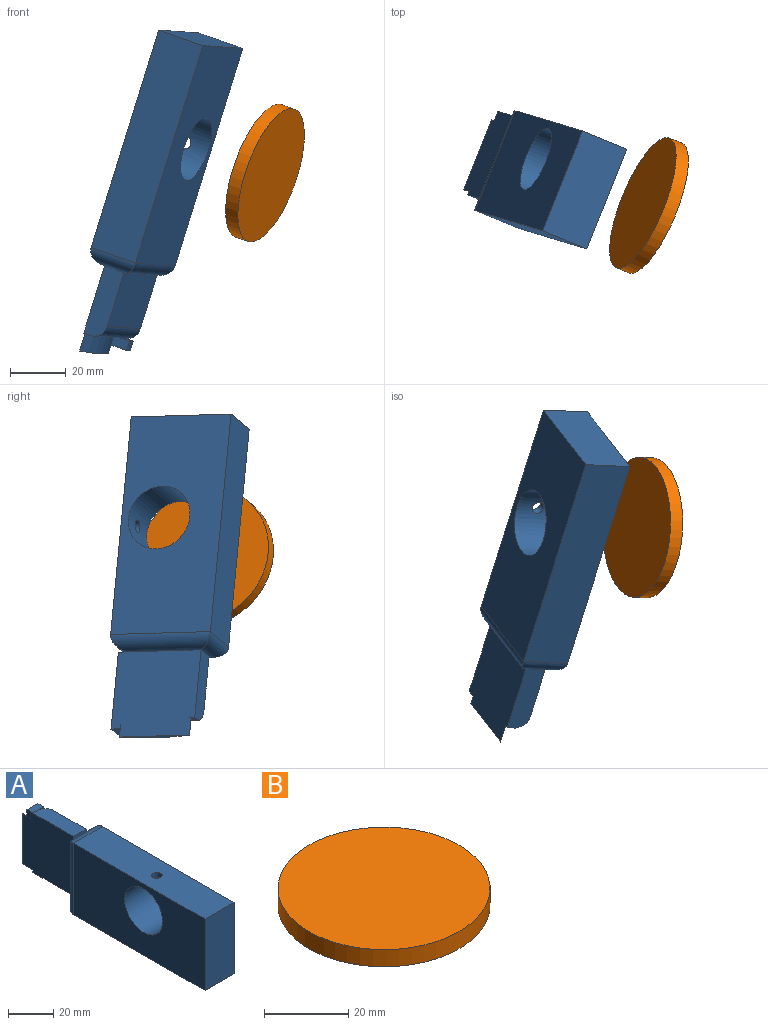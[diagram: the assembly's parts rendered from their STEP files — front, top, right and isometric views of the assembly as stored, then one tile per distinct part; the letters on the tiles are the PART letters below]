
ASSEMBLY  parts=2 mates=1
PART A: 26 faces, bbox 18.1x119.4x38.6 mm
  f0: plane 32.16x32.08mm, normal (-1,0,0), area 1009.8mm2, adj f1,f3,f4,f5,f13,f18,f20,f21
  f1: plane 6.69x3.63mm, normal (0,1,0), area 24.2mm2, adj f0,f2,f23,f24,f25
  f2: plane 3.64x3.63mm, normal (1,0,0), area 13.2mm2, adj f1,f3,f24,f25
  f3: plane 6.69x3.63mm, normal (0,-1,0), area 14.1mm2, adj f0,f2,f19,f21,f24,f25
  f4: plane 27.11x2.01mm, normal (0,1,0), area 37.6mm2, adj f0,f22,f23
  f5: plane 28.45x2.83mm, normal (0,1,0), area 42.8mm2, adj f0,f18,f19,f22,f24
  f6: plane 82.14x38.61mm, normal (-1,0,0), area 2730.3mm2, adj f7,f9,f10,f11,f13
  f7: plane 38.61x18.07mm, normal (0,-1,0), area 697.6mm2, adj f6,f8,f9,f10
  f8: plane 82.14x38.61mm, normal (1,0,0), area 2730.3mm2, adj f7,f9,f10,f11,f16
  f9: plane 82.14x18.07mm, normal (0,0,1), area 1467.3mm2, adj f6,f7,f8,f12,f14
  f10: plane 82.14x18.07mm, normal (0,0,-1), area 1483.9mm2, adj f6,f7,f8,f15
  f11: cylinder r=11.85mm len=23.7mm, axis (-1,0,0), area 1328.4mm2, adj f6,f8,f12
  f12: cylinder r=2.3mm len=4.6mm, axis (0,0,1), area 40.8mm2, adj f9,f11
  f13: cylinder r=5.08mm len=38.61mm, axis (0,0,1), area 278.6mm2, adj f0,f6,f14,f15
  f14: cylinder r=5.08mm len=18.07mm, axis (1,0,0), area 114.7mm2, adj f9,f13,f16,f20
  f15: cylinder r=5.08mm len=18.07mm, axis (-1,0,0), area 114.7mm2, adj f10,f13,f16,f18
  f16: cylinder r=5.08mm len=38.61mm, axis (0,0,-1), area 278.6mm2, adj f8,f14,f15,f17
  f17: plane 32.03x20.32mm, normal (1,0,0), area 650.8mm2, adj f16,f18,f19,f20,f21
  f18: plane 25.4x7.91mm, normal (0,0,-1), area 195.3mm2, adj f0,f5,f15,f17,f19
  f19: cylinder r=5.08mm len=32.03mm, axis (0,0,1), area 255.6mm2, adj f3,f5,f17,f18,f21
  f20: plane 7.91x3.57mm, normal (0,-1,0), area 28.3mm2, adj f0,f14,f17,f21
  f21: plane 25.4x7.91mm, normal (0,0,1), area 195.3mm2, adj f0,f3,f17,f19,f20
  f22: cylinder r=49.9mm len=27.09mm, axis (0,-1,0), area 185.5mm2, adj f0,f4,f5,f23,f24
  f23: plane 3.12x0.27mm, normal (0.07,0,1), area 0.8mm2, adj f0,f1,f4,f22
  f24: plane 6.42x3.64mm, normal (0,0,-1), area 23.4mm2, adj f1,f2,f3,f5,f22
  f25: plane 6.69x3.64mm, normal (0,0,1), area 24.3mm2, adj f0,f1,f2,f3
PART B: 3 faces, bbox 50.4x50.4x5 mm
  f0: cylinder r=25.19mm len=50.39mm, axis (0,0,1), area 791.5mm2, adj f1,f2
  f1: plane 50.39x50.39mm, normal (0,0,1), area 1994mm2, adj f0
  f2: plane 50.39x50.39mm, normal (0,0,-1), area 1994mm2, adj f0
PLACE A rot(axis=(-0.94,0.34,-0.03),91.6deg) t=(140.97,77.27,75.12)mm
PLACE B rot(axis=(0.84,0.23,0.5),137.7deg) t=(125.61,81.13,0.97)mm
MATE cylindrical A.f11 <-> B.f0  axis (0.88,-0.36,-0.31) through (122.98,109.44,43.39)mm
